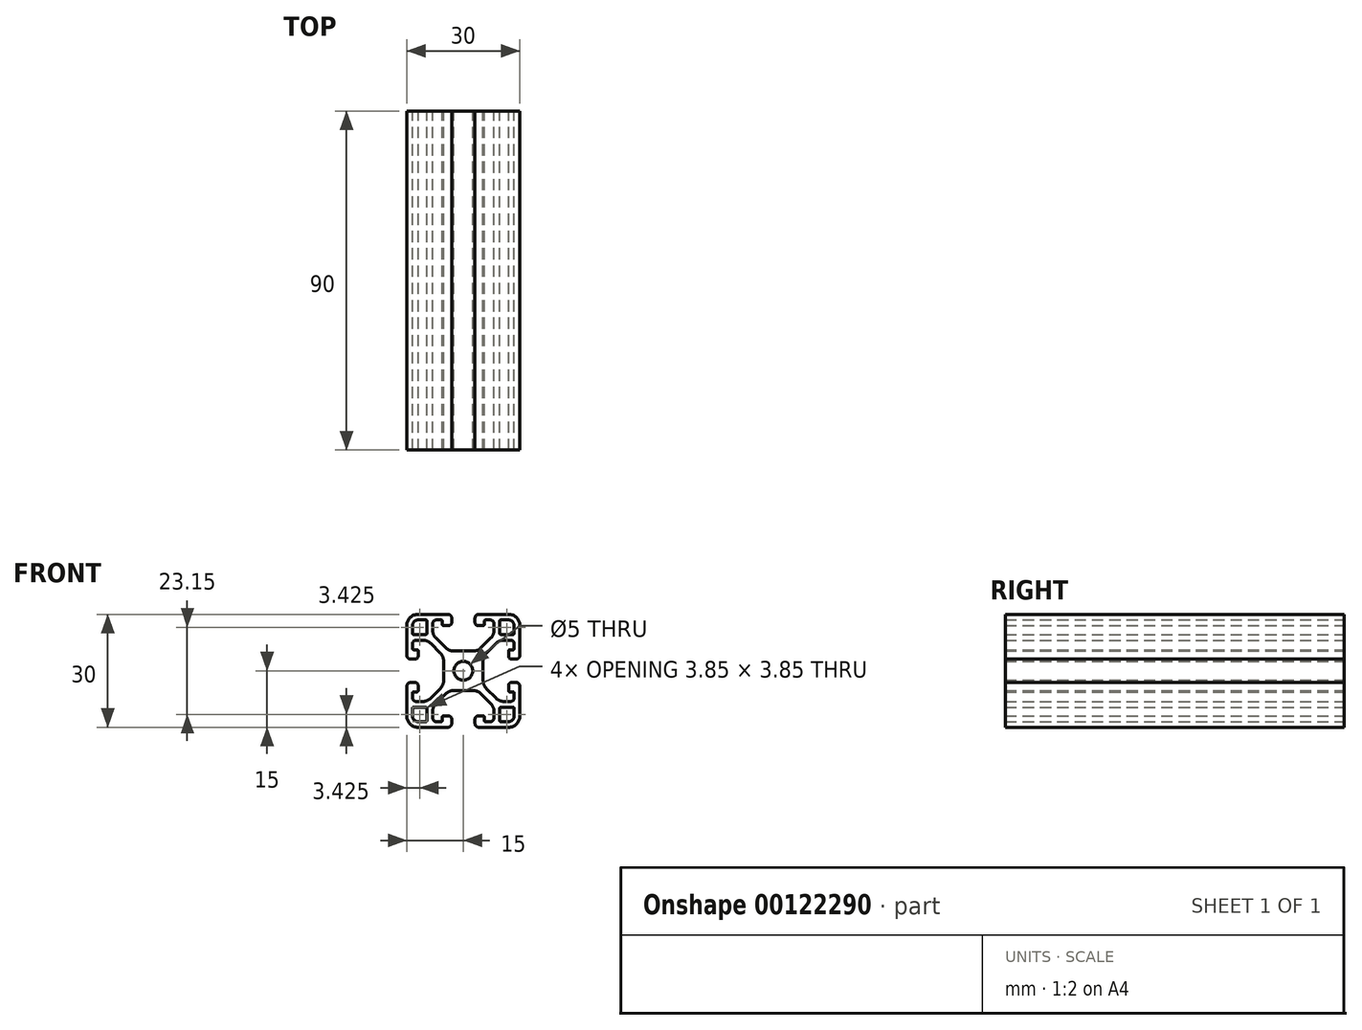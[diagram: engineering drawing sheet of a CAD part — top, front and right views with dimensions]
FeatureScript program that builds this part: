
annotation { "Feature Type Name" : "Feature", "Feature Type Description" : "" }
export const myFeature = defineFeature(function(context is Context, id is Id, definition is map)
    precondition{}
    {
        {
            var Q0;
            Q0=qCreatedBy(makeId("Front.planeOp"),FACE);
            var sketch = newSketch(context, id + "F0", { "sketchPlane" : qUnion([Q0])});
            skLineSegment(sketch, "E0", {"start": v(0, 5.25) * mm, "end": v(2.6, 5.25) * mm});
            skLineSegment(sketch, "E1", {"start": v(4.71, 6.13) * mm, "end": v(7.27, 8.69) * mm});
            skLineSegment(sketch, "E2", {"start": v(8.15, 10.8) * mm, "end": v(8.15, 12.5) * mm});
            skLineSegment(sketch, "E3", {"start": v(7.15, 13.5) * mm, "end": v(5.9, 13.5) * mm});
            skLineSegment(sketch, "E4", {"start": v(5.6, 13.2) * mm, "end": v(5.6, 12.3) * mm});
            skLineSegment(sketch, "E5", {"start": v(5.3, 12) * mm, "end": v(3.9, 12) * mm});
            skLineSegment(sketch, "E6", {"start": v(3.1, 12.8) * mm, "end": v(3.1, 14) * mm});
            skLineSegment(sketch, "E7", {"start": v(4.1, 15) * mm, "end": v(12, 15) * mm});
            skPoint(sketch, "E8.visualSharp", {"position": v(3.84, 5.25) * mm});
            skArc(sketch, "E8.filletArc", {"start": v(2.6, 5.25) * mm, "mid": v(3.74, 5.48) * mm, "end": v(4.71, 6.13) * mm});
            skPoint(sketch, "E9.visualSharp", {"position": v(8.15, 9.56) * mm});
            skArc(sketch, "E9.filletArc", {"start": v(7.27, 8.69) * mm, "mid": v(7.92, 9.66) * mm, "end": v(8.15, 10.8) * mm});
            skPoint(sketch, "E10.visualSharp", {"position": v(8.15, 13.5) * mm});
            skArc(sketch, "E10.filletArc", {"start": v(8.15, 12.5) * mm, "mid": v(7.86, 13.2) * mm, "end": v(7.15, 13.5) * mm});
            skPoint(sketch, "E11.visualSharp", {"position": v(5.6, 13.5) * mm});
            skArc(sketch, "E11.filletArc", {"start": v(5.9, 13.5) * mm, "mid": v(5.69, 13.41) * mm, "end": v(5.6, 13.2) * mm});
            skPoint(sketch, "E12.visualSharp", {"position": v(5.6, 12) * mm});
            skArc(sketch, "E12.filletArc", {"start": v(5.3, 12) * mm, "mid": v(5.51, 12.09) * mm, "end": v(5.6, 12.3) * mm});
            skPoint(sketch, "E13.visualSharp", {"position": v(3.1, 12) * mm});
            skArc(sketch, "E13.filletArc", {"start": v(3.1, 12.8) * mm, "mid": v(3.33, 12.23) * mm, "end": v(3.9, 12) * mm});
            skPoint(sketch, "E14.visualSharp", {"position": v(3.1, 15) * mm});
            skArc(sketch, "E14.filletArc", {"start": v(4.1, 15) * mm, "mid": v(3.4, 14.7) * mm, "end": v(3.1, 14) * mm});
            skArc(sketch, "E15.MirrorCS", {"start": v(12, 5.3) * mm, "mid": v(12.09, 5.51) * mm, "end": v(12.3, 5.6) * mm});
            skArc(sketch, "E16.MirrorCS", {"start": v(13.5, 5.9) * mm, "mid": v(13.41, 5.69) * mm, "end": v(13.2, 5.6) * mm});
            skPoint(sketch, "E17.MirrorP", {"position": v(13.5, 5.6) * mm});
            skLineSegment(sketch, "E18.MirrorCS", {"start": v(5.25, 0) * mm, "end": v(5.25, 2.6) * mm});
            skLineSegment(sketch, "E19.MirrorCS", {"start": v(6.13, 4.71) * mm, "end": v(8.69, 7.27) * mm});
            skPoint(sketch, "E20.MirrorP", {"position": v(13.5, 8.15) * mm});
            skLineSegment(sketch, "E21.MirrorCS", {"start": v(10.8, 8.15) * mm, "end": v(12.5, 8.15) * mm});
            skLineSegment(sketch, "E22.MirrorCS", {"start": v(13.5, 7.15) * mm, "end": v(13.5, 5.9) * mm});
            skPoint(sketch, "E23.MirrorP", {"position": v(9.56, 8.15) * mm});
            skLineSegment(sketch, "E24.MirrorCS", {"start": v(13.2, 5.6) * mm, "end": v(12.3, 5.6) * mm});
            skArc(sketch, "E25.MirrorCS", {"start": v(15, 4.1) * mm, "mid": v(14.7, 3.4) * mm, "end": v(14, 3.1) * mm});
            skArc(sketch, "E26.MirrorCS", {"start": v(12.8, 3.1) * mm, "mid": v(12.23, 3.33) * mm, "end": v(12, 3.9) * mm});
            skPoint(sketch, "E27.MirrorP", {"position": v(12, 5.6) * mm});
            skLineSegment(sketch, "E28.MirrorCS", {"start": v(12, 5.3) * mm, "end": v(12, 3.9) * mm});
            skPoint(sketch, "E29.MirrorP", {"position": v(5.25, 3.84) * mm});
            skLineSegment(sketch, "E30.MirrorCS", {"start": v(15, 4.1) * mm, "end": v(15, 12) * mm});
            skLineSegment(sketch, "E31.MirrorCS", {"start": v(12.8, 3.1) * mm, "end": v(14, 3.1) * mm});
            skArc(sketch, "E32.MirrorCS", {"start": v(5.25, 2.6) * mm, "mid": v(5.48, 3.74) * mm, "end": v(6.13, 4.71) * mm});
            skArc(sketch, "E33.MirrorCS", {"start": v(12.5, 8.15) * mm, "mid": v(13.2, 7.86) * mm, "end": v(13.5, 7.15) * mm});
            skArc(sketch, "E34.MirrorCS", {"start": v(8.69, 7.27) * mm, "mid": v(9.66, 7.92) * mm, "end": v(10.8, 8.15) * mm});
            skPoint(sketch, "E35.MirrorP", {"position": v(15, 3.1) * mm});
            skPoint(sketch, "E36.MirrorP", {"position": v(12, 3.1) * mm});
            skArc(sketch, "E37.MirrorCS", {"start": v(-5.9, 13.5) * mm, "mid": v(-5.69, 13.41) * mm, "end": v(-5.6, 13.2) * mm});
            skLineSegment(sketch, "E38.MirrorCS", {"start": v(-5.6, 13.2) * mm, "end": v(-5.6, 12.3) * mm});
            skArc(sketch, "E39.MirrorCS", {"start": v(-5.3, 12) * mm, "mid": v(-5.51, 12.09) * mm, "end": v(-5.6, 12.3) * mm});
            skArc(sketch, "E40.MirrorCS", {"start": v(-12, 5.3) * mm, "mid": v(-12.09, 5.51) * mm, "end": v(-12.3, 5.6) * mm});
            skLineSegment(sketch, "E41.MirrorCS", {"start": v(-13.2, 5.6) * mm, "end": v(-12.3, 5.6) * mm});
            skArc(sketch, "E42.MirrorCS", {"start": v(-13.5, 5.9) * mm, "mid": v(-13.41, 5.69) * mm, "end": v(-13.2, 5.6) * mm});
            skArc(sketch, "E43.MirrorCS", {"start": v(-12.5, 8.15) * mm, "mid": v(-13.2, 7.86) * mm, "end": v(-13.5, 7.15) * mm});
            skArc(sketch, "E44.MirrorCS", {"start": v(-15, 4.1) * mm, "mid": v(-14.7, 3.4) * mm, "end": v(-14, 3.1) * mm});
            skArc(sketch, "E45.MirrorCS", {"start": v(-8.15, 12.5) * mm, "mid": v(-7.86, 13.2) * mm, "end": v(-7.15, 13.5) * mm});
            skLineSegment(sketch, "E46.MirrorCS", {"start": v(-5.3, 12) * mm, "end": v(-3.9, 12) * mm});
            skLineSegment(sketch, "E47.MirrorCS", {"start": v(-7.15, 13.5) * mm, "end": v(-5.9, 13.5) * mm});
            skArc(sketch, "E48.MirrorCS", {"start": v(-3.1, 12.8) * mm, "mid": v(-3.33, 12.23) * mm, "end": v(-3.9, 12) * mm});
            skArc(sketch, "E49.MirrorCS", {"start": v(-4.1, 15) * mm, "mid": v(-3.4, 14.7) * mm, "end": v(-3.1, 14) * mm});
            skArc(sketch, "E50.MirrorCS", {"start": v(-12.8, 3.1) * mm, "mid": v(-12.23, 3.33) * mm, "end": v(-12, 3.9) * mm});
            skPoint(sketch, "E51.MirrorP", {"position": v(-12, 3.1) * mm});
            skLineSegment(sketch, "E52.MirrorCS", {"start": v(-5.25, 0) * mm, "end": v(-5.25, 2.6) * mm});
            skLineSegment(sketch, "E53.MirrorCS", {"start": v(-10.8, 8.15) * mm, "end": v(-12.5, 8.15) * mm});
            skPoint(sketch, "E54.MirrorP", {"position": v(-9.56, 8.15) * mm});
            skLineSegment(sketch, "E55.MirrorCS", {"start": v(-12, 5.3) * mm, "end": v(-12, 3.9) * mm});
            skLineSegment(sketch, "E56.MirrorCS", {"start": v(-12.8, 3.1) * mm, "end": v(-14, 3.1) * mm});
            skArc(sketch, "E57.MirrorCS", {"start": v(-7.27, 8.69) * mm, "mid": v(-7.92, 9.66) * mm, "end": v(-8.15, 10.8) * mm});
            skArc(sketch, "E58.MirrorCS", {"start": v(-2.6, 5.25) * mm, "mid": v(-3.74, 5.48) * mm, "end": v(-4.71, 6.13) * mm});
            skLineSegment(sketch, "E59.MirrorCS", {"start": v(-4.1, 15) * mm, "end": v(-12, 15) * mm});
            skLineSegment(sketch, "E60.MirrorCS", {"start": v(-3.1, 12.8) * mm, "end": v(-3.1, 14) * mm});
            skPoint(sketch, "E61.MirrorP", {"position": v(-8.15, 9.56) * mm});
            skPoint(sketch, "E62.MirrorP", {"position": v(-8.15, 13.5) * mm});
            skPoint(sketch, "E63.MirrorP", {"position": v(-5.25, 3.84) * mm});
            skLineSegment(sketch, "E64.MirrorCS", {"start": v(-8.15, 10.8) * mm, "end": v(-8.15, 12.5) * mm});
            skPoint(sketch, "E65.MirrorP", {"position": v(-15, 3.1) * mm});
            skPoint(sketch, "E66.MirrorP", {"position": v(-5.6, 13.5) * mm});
            skPoint(sketch, "E67.MirrorP", {"position": v(-3.1, 15) * mm});
            skLineSegment(sketch, "E68.MirrorCS", {"start": v(-6.13, 4.71) * mm, "end": v(-8.69, 7.27) * mm});
            skLineSegment(sketch, "E69.MirrorCS", {"start": v(-4.71, 6.13) * mm, "end": v(-7.27, 8.69) * mm});
            skArc(sketch, "E70.MirrorCS", {"start": v(-8.69, 7.27) * mm, "mid": v(-9.66, 7.92) * mm, "end": v(-10.8, 8.15) * mm});
            skLineSegment(sketch, "E71.MirrorCS", {"start": v(-13.5, 7.15) * mm, "end": v(-13.5, 5.9) * mm});
            skPoint(sketch, "E72.MirrorP", {"position": v(-13.5, 8.15) * mm});
            skPoint(sketch, "E73.MirrorP", {"position": v(-3.1, 12) * mm});
            skPoint(sketch, "E74.MirrorP", {"position": v(-3.84, 5.25) * mm});
            skPoint(sketch, "E75.MirrorP", {"position": v(-5.6, 12) * mm});
            skLineSegment(sketch, "E76.MirrorCS", {"start": v(0, 5.25) * mm, "end": v(-2.6, 5.25) * mm});
            skLineSegment(sketch, "E77.MirrorCS", {"start": v(-15, 4.1) * mm, "end": v(-15, 12) * mm});
            skArc(sketch, "E78.MirrorCS", {"start": v(-5.25, 2.6) * mm, "mid": v(-5.48, 3.74) * mm, "end": v(-6.13, 4.71) * mm});
            skPoint(sketch, "E79.MirrorP", {"position": v(-12, 5.6) * mm});
            skPoint(sketch, "E80.MirrorP", {"position": v(-13.5, 5.6) * mm});
            skLineSegment(sketch, "E81.MirrorCS", {"start": v(5.6, -13.2) * mm, "end": v(5.6, -12.3) * mm});
            skArc(sketch, "E82.MirrorCS", {"start": v(5.9, -13.5) * mm, "mid": v(5.69, -13.41) * mm, "end": v(5.6, -13.2) * mm});
            skArc(sketch, "E83.MirrorCS", {"start": v(5.3, -12) * mm, "mid": v(5.51, -12.09) * mm, "end": v(5.6, -12.3) * mm});
            skArc(sketch, "E84.MirrorCS", {"start": v(-12, -5.3) * mm, "mid": v(-12.09, -5.51) * mm, "end": v(-12.3, -5.6) * mm});
            skArc(sketch, "E85.MirrorCS", {"start": v(-5.9, -13.5) * mm, "mid": v(-5.69, -13.41) * mm, "end": v(-5.6, -13.2) * mm});
            skLineSegment(sketch, "E86.MirrorCS", {"start": v(13.2, -5.6) * mm, "end": v(12.3, -5.6) * mm});
            skArc(sketch, "E87.MirrorCS", {"start": v(-5.3, -12) * mm, "mid": v(-5.51, -12.09) * mm, "end": v(-5.6, -12.3) * mm});
            skArc(sketch, "E88.MirrorCS", {"start": v(13.5, -5.9) * mm, "mid": v(13.41, -5.69) * mm, "end": v(13.2, -5.6) * mm});
            skLineSegment(sketch, "E89.MirrorCS", {"start": v(-5.6, -13.2) * mm, "end": v(-5.6, -12.3) * mm});
            skArc(sketch, "E90.MirrorCS", {"start": v(-13.5, -5.9) * mm, "mid": v(-13.41, -5.69) * mm, "end": v(-13.2, -5.6) * mm});
            skArc(sketch, "E91.MirrorCS", {"start": v(12, -5.3) * mm, "mid": v(12.09, -5.51) * mm, "end": v(12.3, -5.6) * mm});
            skLineSegment(sketch, "E92.MirrorCS", {"start": v(-13.2, -5.6) * mm, "end": v(-12.3, -5.6) * mm});
            skArc(sketch, "E93.MirrorCS", {"start": v(-15, -4.1) * mm, "mid": v(-14.7, -3.4) * mm, "end": v(-14, -3.1) * mm});
            skArc(sketch, "E94.MirrorCS", {"start": v(-12.5, -8.15) * mm, "mid": v(-13.2, -7.86) * mm, "end": v(-13.5, -7.15) * mm});
            skArc(sketch, "E95.MirrorCS", {"start": v(12.8, -3.1) * mm, "mid": v(12.23, -3.33) * mm, "end": v(12, -3.9) * mm});
            skArc(sketch, "E96.MirrorCS", {"start": v(-12.8, -3.1) * mm, "mid": v(-12.23, -3.33) * mm, "end": v(-12, -3.9) * mm});
            skLineSegment(sketch, "E97.MirrorCS", {"start": v(7.15, -13.5) * mm, "end": v(5.9, -13.5) * mm});
            skLineSegment(sketch, "E98.MirrorCS", {"start": v(5.3, -12) * mm, "end": v(3.9, -12) * mm});
            skArc(sketch, "E99.MirrorCS", {"start": v(8.15, -12.5) * mm, "mid": v(7.86, -13.2) * mm, "end": v(7.15, -13.5) * mm});
            skArc(sketch, "E100.MirrorCS", {"start": v(-4.1, -15) * mm, "mid": v(-3.4, -14.7) * mm, "end": v(-3.1, -14) * mm});
            skArc(sketch, "E101.MirrorCS", {"start": v(-3.1, -12.8) * mm, "mid": v(-3.33, -12.23) * mm, "end": v(-3.9, -12) * mm});
            skArc(sketch, "E102.MirrorCS", {"start": v(15, -4.1) * mm, "mid": v(14.7, -3.4) * mm, "end": v(14, -3.1) * mm});
            skArc(sketch, "E103.MirrorCS", {"start": v(-8.15, -12.5) * mm, "mid": v(-7.86, -13.2) * mm, "end": v(-7.15, -13.5) * mm});
            skArc(sketch, "E104.MirrorCS", {"start": v(12.5, -8.15) * mm, "mid": v(13.2, -7.86) * mm, "end": v(13.5, -7.15) * mm});
            skArc(sketch, "E105.MirrorCS", {"start": v(3.1, -12.8) * mm, "mid": v(3.33, -12.23) * mm, "end": v(3.9, -12) * mm});
            skArc(sketch, "E106.MirrorCS", {"start": v(4.1, -15) * mm, "mid": v(3.4, -14.7) * mm, "end": v(3.1, -14) * mm});
            skPoint(sketch, "E107.MirrorP", {"position": v(-3.1, -15) * mm});
            skArc(sketch, "E108.MirrorCS", {"start": v(-2.6, -5.25) * mm, "mid": v(-3.74, -5.48) * mm, "end": v(-4.71, -6.13) * mm});
            skLineSegment(sketch, "E109.MirrorCS", {"start": v(5.25, 0) * mm, "end": v(5.25, -2.6) * mm});
            skLineSegment(sketch, "E110.MirrorCS", {"start": v(-6.13, -4.71) * mm, "end": v(-8.69, -7.27) * mm});
            skLineSegment(sketch, "E111.MirrorCS", {"start": v(-12, -5.3) * mm, "end": v(-12, -3.9) * mm});
            skLineSegment(sketch, "E112.MirrorCS", {"start": v(12, -5.3) * mm, "end": v(12, -3.9) * mm});
            skLineSegment(sketch, "E113.MirrorCS", {"start": v(-7.15, -13.5) * mm, "end": v(-5.9, -13.5) * mm});
            skLineSegment(sketch, "E114.MirrorCS", {"start": v(-13.5, -7.15) * mm, "end": v(-13.5, -5.9) * mm});
            skPoint(sketch, "E115.MirrorP", {"position": v(5.6, -12) * mm});
            skPoint(sketch, "E116.MirrorP", {"position": v(12, -5.6) * mm});
            skPoint(sketch, "E117.MirrorP", {"position": v(-5.25, -3.84) * mm});
            skPoint(sketch, "E118.MirrorP", {"position": v(3.1, -15) * mm});
            skPoint(sketch, "E119.MirrorP", {"position": v(-5.6, -13.5) * mm});
            skArc(sketch, "E120.MirrorCS", {"start": v(-7.27, -8.69) * mm, "mid": v(-7.92, -9.66) * mm, "end": v(-8.15, -10.8) * mm});
            skPoint(sketch, "E121.MirrorP", {"position": v(8.15, -9.56) * mm});
            skPoint(sketch, "E122.MirrorP", {"position": v(9.56, -8.15) * mm});
            skPoint(sketch, "E123.MirrorP", {"position": v(-3.1, -12) * mm});
            skArc(sketch, "E124.MirrorCS", {"start": v(8.69, -7.27) * mm, "mid": v(9.66, -7.92) * mm, "end": v(10.8, -8.15) * mm});
            skLineSegment(sketch, "E125.MirrorCS", {"start": v(-8.15, -10.8) * mm, "end": v(-8.15, -12.5) * mm});
            skLineSegment(sketch, "E126.MirrorCS", {"start": v(-10.8, -8.15) * mm, "end": v(-12.5, -8.15) * mm});
            skLineSegment(sketch, "E127.MirrorCS", {"start": v(13.5, -7.15) * mm, "end": v(13.5, -5.9) * mm});
            skPoint(sketch, "E128.MirrorP", {"position": v(-9.56, -8.15) * mm});
            skPoint(sketch, "E129.MirrorP", {"position": v(-13.5, -5.6) * mm});
            skLineSegment(sketch, "E130.MirrorCS", {"start": v(-5.3, -12) * mm, "end": v(-3.9, -12) * mm});
            skArc(sketch, "E131.MirrorCS", {"start": v(-8.69, -7.27) * mm, "mid": v(-9.66, -7.92) * mm, "end": v(-10.8, -8.15) * mm});
            skArc(sketch, "E132.MirrorCS", {"start": v(5.25, -2.6) * mm, "mid": v(5.48, -3.74) * mm, "end": v(6.13, -4.71) * mm});
            skArc(sketch, "E133.MirrorCS", {"start": v(-5.25, -2.6) * mm, "mid": v(-5.48, -3.74) * mm, "end": v(-6.13, -4.71) * mm});
            skPoint(sketch, "E134.MirrorP", {"position": v(12, -3.1) * mm});
            skPoint(sketch, "E135.MirrorP", {"position": v(-8.15, -13.5) * mm});
            skPoint(sketch, "E136.MirrorP", {"position": v(-5.6, -12) * mm});
            skPoint(sketch, "E137.MirrorP", {"position": v(8.15, -13.5) * mm});
            skPoint(sketch, "E138.MirrorP", {"position": v(-3.84, -5.25) * mm});
            skPoint(sketch, "E139.MirrorP", {"position": v(-8.15, -9.56) * mm});
            skPoint(sketch, "E140.MirrorP", {"position": v(15, -3.1) * mm});
            skLineSegment(sketch, "E141.MirrorCS", {"start": v(3.1, -12.8) * mm, "end": v(3.1, -14) * mm});
            skLineSegment(sketch, "E142.MirrorCS", {"start": v(4.1, -15) * mm, "end": v(12, -15) * mm});
            skArc(sketch, "E143.MirrorCS", {"start": v(2.6, -5.25) * mm, "mid": v(3.74, -5.48) * mm, "end": v(4.71, -6.13) * mm});
            skArc(sketch, "E144.MirrorCS", {"start": v(7.27, -8.69) * mm, "mid": v(7.92, -9.66) * mm, "end": v(8.15, -10.8) * mm});
            skPoint(sketch, "E145.MirrorP", {"position": v(-15, -3.1) * mm});
            skLineSegment(sketch, "E146.MirrorCS", {"start": v(-15, -4.1) * mm, "end": v(-15, -12) * mm});
            skLineSegment(sketch, "E147.MirrorCS", {"start": v(0, -5.25) * mm, "end": v(-2.6, -5.25) * mm});
            skLineSegment(sketch, "E148.MirrorCS", {"start": v(15, -4.1) * mm, "end": v(15, -12) * mm});
            skLineSegment(sketch, "E149.MirrorCS", {"start": v(12.8, -3.1) * mm, "end": v(14, -3.1) * mm});
            skLineSegment(sketch, "E150.MirrorCS", {"start": v(-4.71, -6.13) * mm, "end": v(-7.27, -8.69) * mm});
            skPoint(sketch, "E151.MirrorP", {"position": v(5.6, -13.5) * mm});
            skPoint(sketch, "E152.MirrorP", {"position": v(-12, -5.6) * mm});
            skPoint(sketch, "E153.MirrorP", {"position": v(5.25, -3.84) * mm});
            skPoint(sketch, "E154.MirrorP", {"position": v(-12, -3.1) * mm});
            skLineSegment(sketch, "E155.MirrorCS", {"start": v(10.8, -8.15) * mm, "end": v(12.5, -8.15) * mm});
            skPoint(sketch, "E156.MirrorP", {"position": v(3.84, -5.25) * mm});
            skPoint(sketch, "E157.MirrorP", {"position": v(13.5, -5.6) * mm});
            skPoint(sketch, "E158.MirrorP", {"position": v(-13.5, -8.15) * mm});
            skPoint(sketch, "E159.MirrorP", {"position": v(13.5, -8.15) * mm});
            skLineSegment(sketch, "E160.MirrorCS", {"start": v(0, -5.25) * mm, "end": v(2.6, -5.25) * mm});
            skLineSegment(sketch, "E161.MirrorCS", {"start": v(6.13, -4.71) * mm, "end": v(8.69, -7.27) * mm});
            skLineSegment(sketch, "E162.MirrorCS", {"start": v(-3.1, -12.8) * mm, "end": v(-3.1, -14) * mm});
            skLineSegment(sketch, "E163.MirrorCS", {"start": v(-5.25, 0) * mm, "end": v(-5.25, -2.6) * mm});
            skLineSegment(sketch, "E164.MirrorCS", {"start": v(-4.1, -15) * mm, "end": v(-12, -15) * mm});
            skLineSegment(sketch, "E165.MirrorCS", {"start": v(4.71, -6.13) * mm, "end": v(7.27, -8.69) * mm});
            skLineSegment(sketch, "E166.MirrorCS", {"start": v(-12.8, -3.1) * mm, "end": v(-14, -3.1) * mm});
            skLineSegment(sketch, "E167.MirrorCS", {"start": v(8.15, -10.8) * mm, "end": v(8.15, -12.5) * mm});
            skPoint(sketch, "E168.MirrorP", {"position": v(3.1, -12) * mm});
            skCircle(sketch, "E169", {"center": v(0, 0) * mm, "radius": 2.5 * mm});
            skLineSegment(sketch, "E170.bottom", {"start": v(9.95, 13.5) * mm, "end": v(12, 13.5) * mm});
            skLineSegment(sketch, "E170.top", {"start": v(9.95, 9.65) * mm, "end": v(13.2, 9.65) * mm});
            skLineSegment(sketch, "E170.left", {"start": v(9.65, 13.2) * mm, "end": v(9.65, 9.95) * mm});
            skLineSegment(sketch, "E170.right", {"start": v(13.5, 12) * mm, "end": v(13.5, 9.95) * mm});
            skPoint(sketch, "E171.visualSharp", {"position": v(9.65, 9.65) * mm});
            skArc(sketch, "E171.filletArc", {"start": v(9.65, 9.95) * mm, "mid": v(9.74, 9.74) * mm, "end": v(9.95, 9.65) * mm});
            skPoint(sketch, "E172.visualSharp", {"position": v(13.5, 9.65) * mm});
            skArc(sketch, "E172.filletArc", {"start": v(13.2, 9.65) * mm, "mid": v(13.41, 9.74) * mm, "end": v(13.5, 9.95) * mm});
            skPoint(sketch, "E173.visualSharp", {"position": v(9.65, 13.5) * mm});
            skArc(sketch, "E173.filletArc", {"start": v(9.95, 13.5) * mm, "mid": v(9.74, 13.41) * mm, "end": v(9.65, 13.2) * mm});
            skPoint(sketch, "E174.visualSharp", {"position": v(13.5, 13.5) * mm});
            skArc(sketch, "E174.filletArc", {"start": v(13.5, 12) * mm, "mid": v(13.06, 13.06) * mm, "end": v(12, 13.5) * mm});
            skArc(sketch, "E175.MirrorCS", {"start": v(-13.2, 9.65) * mm, "mid": v(-13.41, 9.74) * mm, "end": v(-13.5, 9.95) * mm});
            skArc(sketch, "E176.MirrorCS", {"start": v(-9.65, 9.95) * mm, "mid": v(-9.74, 9.74) * mm, "end": v(-9.95, 9.65) * mm});
            skArc(sketch, "E177.MirrorCS", {"start": v(-9.95, 13.5) * mm, "mid": v(-9.74, 13.41) * mm, "end": v(-9.65, 13.2) * mm});
            skPoint(sketch, "E178.MirrorP", {"position": v(-13.5, 9.65) * mm});
            skPoint(sketch, "E179.MirrorP", {"position": v(-9.65, 9.65) * mm});
            skArc(sketch, "E180.MirrorCS", {"start": v(-13.5, 12) * mm, "mid": v(-13.06, 13.06) * mm, "end": v(-12, 13.5) * mm});
            skLineSegment(sketch, "E181.MirrorCS", {"start": v(-13.5, 12) * mm, "end": v(-13.5, 9.95) * mm});
            skLineSegment(sketch, "E182.MirrorCS", {"start": v(-9.95, 13.5) * mm, "end": v(-12, 13.5) * mm});
            skPoint(sketch, "E183.MirrorP", {"position": v(-13.5, 13.5) * mm});
            skPoint(sketch, "E184.MirrorP", {"position": v(-9.65, 13.5) * mm});
            skLineSegment(sketch, "E185.MirrorCS", {"start": v(-9.95, 9.65) * mm, "end": v(-13.2, 9.65) * mm});
            skLineSegment(sketch, "E186.MirrorCS", {"start": v(-9.65, 13.2) * mm, "end": v(-9.65, 9.95) * mm});
            skArc(sketch, "E187.MirrorCS", {"start": v(-9.65, -9.95) * mm, "mid": v(-9.74, -9.74) * mm, "end": v(-9.95, -9.65) * mm});
            skArc(sketch, "E188.MirrorCS", {"start": v(-9.95, -13.5) * mm, "mid": v(-9.74, -13.41) * mm, "end": v(-9.65, -13.2) * mm});
            skArc(sketch, "E189.MirrorCS", {"start": v(-13.2, -9.65) * mm, "mid": v(-13.41, -9.74) * mm, "end": v(-13.5, -9.95) * mm});
            skArc(sketch, "E190.MirrorCS", {"start": v(-13.5, -12) * mm, "mid": v(-13.06, -13.06) * mm, "end": v(-12, -13.5) * mm});
            skLineSegment(sketch, "E191.MirrorCS", {"start": v(-13.5, -12) * mm, "end": v(-13.5, -9.95) * mm});
            skLineSegment(sketch, "E192.MirrorCS", {"start": v(-9.95, -13.5) * mm, "end": v(-12, -13.5) * mm});
            skLineSegment(sketch, "E193.MirrorCS", {"start": v(-9.95, -9.65) * mm, "end": v(-13.2, -9.65) * mm});
            skLineSegment(sketch, "E194.MirrorCS", {"start": v(-9.65, -13.2) * mm, "end": v(-9.65, -9.95) * mm});
            skPoint(sketch, "E195.MirrorP", {"position": v(-9.65, -13.5) * mm});
            skPoint(sketch, "E196.MirrorP", {"position": v(-13.5, -13.5) * mm});
            skPoint(sketch, "E197.MirrorP", {"position": v(-9.65, -9.65) * mm});
            skPoint(sketch, "E198.MirrorP", {"position": v(-13.5, -9.65) * mm});
            skArc(sketch, "E199.MirrorCS", {"start": v(9.95, -13.5) * mm, "mid": v(9.74, -13.41) * mm, "end": v(9.65, -13.2) * mm});
            skArc(sketch, "E200.MirrorCS", {"start": v(9.65, -9.95) * mm, "mid": v(9.74, -9.74) * mm, "end": v(9.95, -9.65) * mm});
            skArc(sketch, "E201.MirrorCS", {"start": v(13.2, -9.65) * mm, "mid": v(13.41, -9.74) * mm, "end": v(13.5, -9.95) * mm});
            skPoint(sketch, "E202.MirrorP", {"position": v(9.65, -13.5) * mm});
            skPoint(sketch, "E203.MirrorP", {"position": v(9.65, -9.65) * mm});
            skPoint(sketch, "E204.MirrorP", {"position": v(13.5, -9.65) * mm});
            skPoint(sketch, "E205.MirrorP", {"position": v(13.5, -13.5) * mm});
            skLineSegment(sketch, "E206.MirrorCS", {"start": v(9.95, -13.5) * mm, "end": v(12, -13.5) * mm});
            skLineSegment(sketch, "E207.MirrorCS", {"start": v(9.95, -9.65) * mm, "end": v(13.2, -9.65) * mm});
            skLineSegment(sketch, "E208.MirrorCS", {"start": v(13.5, -12) * mm, "end": v(13.5, -9.95) * mm});
            skLineSegment(sketch, "E209.MirrorCS", {"start": v(9.65, -13.2) * mm, "end": v(9.65, -9.95) * mm});
            skArc(sketch, "E210.MirrorCS", {"start": v(13.5, -12) * mm, "mid": v(13.06, -13.06) * mm, "end": v(12, -13.5) * mm});
            skPoint(sketch, "E211.visualSharp", {"position": v(15, 15) * mm});
            skArc(sketch, "E211.filletArc", {"start": v(15, 12) * mm, "mid": v(14.12, 14.12) * mm, "end": v(12, 15) * mm});
            skPoint(sketch, "E212.visualSharp", {"position": v(15, -15) * mm});
            skArc(sketch, "E212.filletArc", {"start": v(12, -15) * mm, "mid": v(14.12, -14.12) * mm, "end": v(15, -12) * mm});
            skPoint(sketch, "E213.visualSharp", {"position": v(-15, -15) * mm});
            skArc(sketch, "E213.filletArc", {"start": v(-15, -12) * mm, "mid": v(-14.12, -14.12) * mm, "end": v(-12, -15) * mm});
            skPoint(sketch, "E214.visualSharp", {"position": v(-15, 15) * mm});
            skArc(sketch, "E214.filletArc", {"start": v(-12, 15) * mm, "mid": v(-14.12, 14.12) * mm, "end": v(-15, 12) * mm});
            skSolve(sketch);
        }
        {
            var Q0;
            Q0 = qSketchRegion(id + "F0", true);
            extrude(context, id + "F1", {"entities" : qUnion([Q0]), "depth" : 90 * mm});
        }
    });
